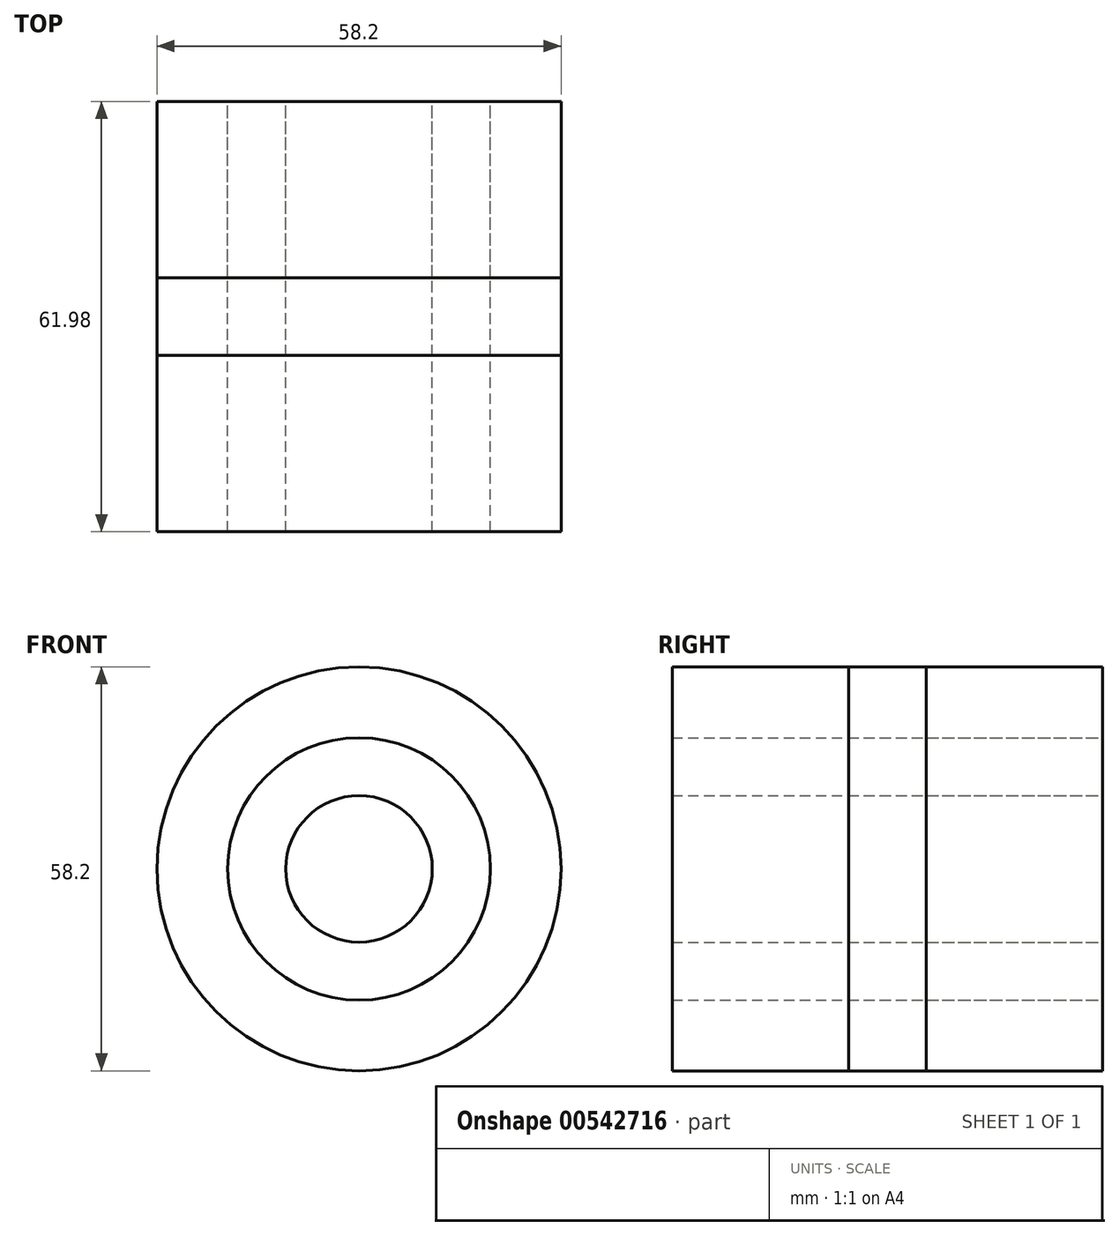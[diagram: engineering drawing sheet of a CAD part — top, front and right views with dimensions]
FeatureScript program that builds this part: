
annotation { "Feature Type Name" : "Feature", "Feature Type Description" : "" }
export const myFeature = defineFeature(function(context is Context, id is Id, definition is map)
    precondition{}
    {
        {
            var Q0;
            Q0=qCreatedBy(makeId("Front.planeOp"),FACE);
            var sketch = newSketch(context, id + "F0", { "sketchPlane" : qUnion([Q0])});
            skCircle(sketch, "E0", {"center": v(0, 0) * mm, "radius": 18.91 * mm});
            skCircle(sketch, "E1", {"center": v(0, 0) * mm, "radius": 29.1 * mm});
            skCircle(sketch, "E2", {"center": v(0, 0) * mm, "radius": 38.73 * mm});
            skSolve(sketch);
        }
        {
            var Q0;
            Q0=makeQuery(id+"F0.imprint","IMPRINT",FACE,{"disambiguationData":[TD([[makeQuery(id+"F0.imprint","IMPRINT",EDGE,{"derivedFrom":sQuery(id+"F0.wireOp",EDGE,"E0")}),-1.0]])]});
            extrude(context, id + "F1", {"entities" : qUnion([Q0]), "depth" : 25.4 * mm, "offsetDistance" : 25.4 * mm});
        }
        {
            var Q0;
            Q0=qCreatedBy(makeId("Front.planeOp"),FACE);
            var sketch = newSketch(context, id + "F2", { "sketchPlane" : qUnion([Q0])});
            skCircle(sketch, "E3", {"center": v(0, 0) * mm, "radius": 10.56 * mm});
            skSolve(sketch);
        }
        {
            var Q0;
            Q0=makeQuery(id+"F2.imprint","IMPRINT",FACE,{"disambiguationData":[TD([[makeQuery(id+"F2.imprint","IMPRINT",EDGE,{"derivedFrom":sQuery(id+"F2.wireOp",EDGE,"E3")}),1.0]])]});
            extrude(context, id + "F3", {"entities" : qUnion([Q0]), "depth" : 25.4 * mm, "offsetDistance" : 25.4 * mm});
        }
        {
            var Q0;
            Q0=makeQuery(id+"F3.opExtrude","CAP_FACE",FACE,{"disambiguationData":[OSD([sQuery(id+"F2.wireOp",EDGE,"E3")])],"isStart":false});
            var Q1;
            Q1=makeQuery(id+"F1.opExtrude","CAP_FACE",FACE,{"disambiguationData":[OSD([sQuery(id+"F0.wireOp",EDGE,"E0"),sQuery(id+"F0.wireOp",EDGE,"E1")])],"isStart":false});
            var Q2;
            Q2=makeQuery(id+"F1.opExtrude","CAP_FACE",FACE,{"disambiguationData":[OSD([sQuery(id+"F0.wireOp",EDGE,"E0"),sQuery(id+"F0.wireOp",EDGE,"E1")])],"isStart":true});
            var Q3;
            Q3=makeQuery(id+"F3.opExtrude","CAP_FACE",FACE,{"disambiguationData":[OSD([sQuery(id+"F2.wireOp",EDGE,"E3")])],"isStart":true});
            extrude(context, id + "F4", {"entities" : qUnion([Q0, Q1, Q2, Q3]), "depth" : 36.58 * mm, "offsetDistance" : 25.4 * mm});
        }
    });
